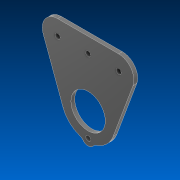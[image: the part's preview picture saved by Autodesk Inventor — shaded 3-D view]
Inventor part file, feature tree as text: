
AUTODESK INVENTOR PART (.ipt)
format: ipt  version: 2022 (Build 260153000, 153)  size: 137,728 bytes
history: native  units: in
note: dims shown in document units (in); Inventor stores cm internally (conversion verified against a paired STEP export)
features: sketch x2, extrude x1, projected_geometry x1
ambient origin geometry x8: Origin, YZ Plane, XZ Plane, XY Plane, X Axis, Y Axis, Z Axis, Center Point
bodies: Solid1 (feature_tree)
feature tree (4):
  extrude  "Extrusion1"  Depth=0.163in
  sketch  "Sketch2"  dims[d5=1.125in d6=1.75in d7=1.0in d8=0.125in d9=0.0in d10=0.25in d11=1.3in d12=0.315in d13=1.625in]
  sketch  "Sketch1"  dims[d0=1.0in d4=0.163in]
  projected_geometry  "Projected Loop1"
